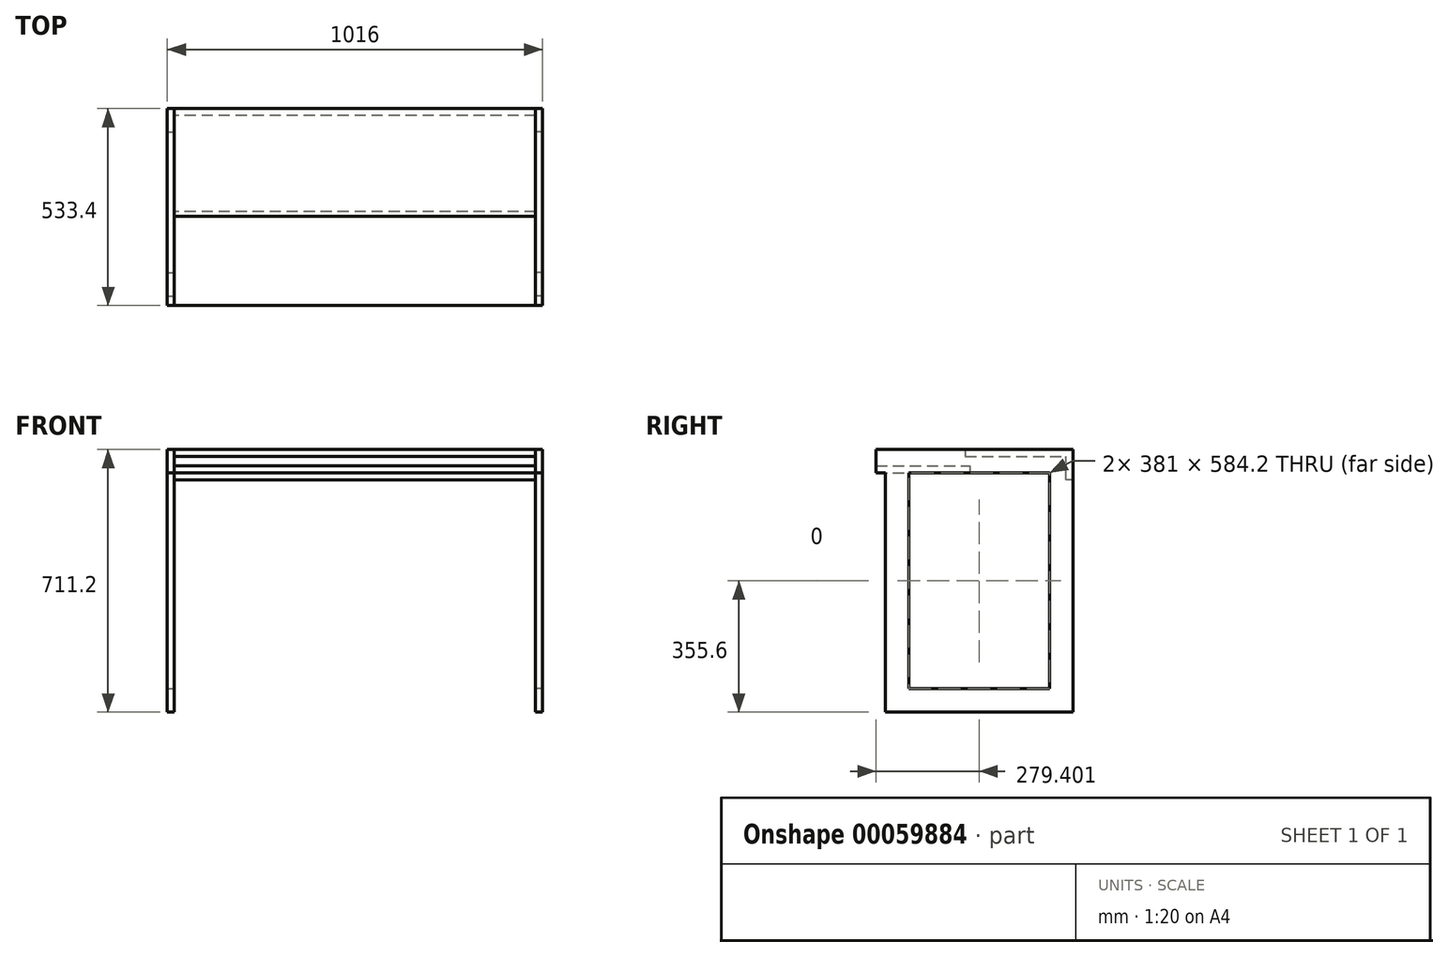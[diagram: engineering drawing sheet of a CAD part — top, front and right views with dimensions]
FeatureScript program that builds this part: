
annotation { "Feature Type Name" : "Feature", "Feature Type Description" : "" }
export const myFeature = defineFeature(function(context is Context, id is Id, definition is map)
    precondition{}
    {
        {
            var Q0;
            Q0=qCreatedBy(makeId("Right.planeOp"),FACE);
            var sketch = newSketch(context, id + "F0", { "sketchPlane" : qUnion([Q0])});
            skLineSegment(sketch, "E0.bottom", {"start": v(182.93, 112.04) * mm, "end": v(475.03, 112.04) * mm});
            skLineSegment(sketch, "E0.top", {"start": v(182.93, 92.99) * mm, "end": v(455.98, 92.99) * mm});
            skLineSegment(sketch, "E0.left", {"start": v(182.93, 112.04) * mm, "end": v(182.93, 92.99) * mm});
            skLineSegment(sketch, "E0.right", {"start": v(475.03, 112.04) * mm, "end": v(475.03, 29.49) * mm});
            skLineSegment(sketch, "E1.bottom", {"start": v(-58.37, 67.59) * mm, "end": v(195.63, 67.59) * mm});
            skLineSegment(sketch, "E1.top", {"start": v(-58.37, 48.54) * mm, "end": v(195.63, 48.54) * mm});
            skLineSegment(sketch, "E1.left", {"start": v(-58.37, 67.59) * mm, "end": v(-58.37, 48.54) * mm});
            skLineSegment(sketch, "E1.right", {"start": v(195.63, 67.59) * mm, "end": v(195.63, 48.54) * mm});
            skLineSegment(sketch, "E2", {"start": v(475.03, 29.49) * mm, "end": v(455.98, 29.49) * mm});
            skLineSegment(sketch, "E3", {"start": v(455.98, 29.49) * mm, "end": v(455.98, 92.99) * mm});
            skSolve(sketch);
        }
        {
            var Q0;
            Q0=makeQuery(id+"F0.imprint","IMPRINT",FACE,{"disambiguationData":[TD([[makeQuery(id+"F0.imprint","IMPRINT",EDGE,{"derivedFrom":sQuery(id+"F0.wireOp",EDGE,"E0.bottom")}),-1.0]])]});
            var Q1;
            Q1=makeQuery(id+"F0.imprint","IMPRINT",FACE,{"disambiguationData":[TD([[makeQuery(id+"F0.imprint","IMPRINT",EDGE,{"derivedFrom":sQuery(id+"F0.wireOp",EDGE,"E1.bottom")}),-1.0]])]});
            extrude(context, id + "F1", {"entities" : qUnion([Q0, Q1]), "depth" : 488.95 * mm, "hasSecondDirection" : true, "secondDirectionOppositeDirection" : true, "secondDirectionDepth" : 488.95 * mm});
        }
        {
            var Q0;
            Q0=makeQuery(id+"F1.opExtrude","CAP_FACE",FACE,{"disambiguationData":[OSD([sQuery(id+"F0.wireOp",EDGE,"E0.bottom"),sQuery(id+"F0.wireOp",EDGE,"E0.top"),sQuery(id+"F0.wireOp",EDGE,"E0.left"),sQuery(id+"F0.wireOp",EDGE,"E0.right"),sQuery(id+"F0.wireOp",EDGE,"E2"),sQuery(id+"F0.wireOp",EDGE,"E3")])],"isStart":false});
            var sketch = newSketch(context, id + "F2", { "sketchPlane" : qUnion([Q0])});
            skLineSegment(sketch, "E4.bottom", {"start": v(-58.37, 112.04) * mm, "end": v(475.03, 112.04) * mm});
            skLineSegment(sketch, "E4.top", {"start": v(-32.97, -599.16) * mm, "end": v(475.03, -599.16) * mm});
            skLineSegment(sketch, "E4.left", {"start": v(-58.37, 112.04) * mm, "end": v(-58.37, 48.54) * mm});
            skLineSegment(sketch, "E4.right", {"start": v(475.03, 112.04) * mm, "end": v(475.03, -599.16) * mm});
            skLineSegment(sketch, "E5.top", {"start": v(30.53, -535.66) * mm, "end": v(411.53, -535.66) * mm});
            skLineSegment(sketch, "E5.left", {"start": v(30.53, 48.54) * mm, "end": v(30.53, -535.66) * mm});
            skLineSegment(sketch, "E5.right", {"start": v(411.53, 48.54) * mm, "end": v(411.53, -535.66) * mm});
            skLineSegment(sketch, "E6", {"start": v(30.53, 48.54) * mm, "end": v(411.53, 48.54) * mm});
            skPoint(sketch, "E7.orphan", {"position": v(30.53, 0) * mm});
            skLineSegment(sketch, "E8", {"start": v(-32.97, -599.16) * mm, "end": v(-32.97, 48.54) * mm});
            skLineSegment(sketch, "E9", {"start": v(-32.97, 48.54) * mm, "end": v(-58.37, 48.54) * mm});
            skSolve(sketch);
        }
        {
            var Q0;
            Q0 = qSketchRegion(id + "F2", true);
            extrude(context, id + "F3", {"entities" : qUnion([Q0]), "depth" : 19.05 * mm});
        }
        {
            var Q0;
            Q0=makeQuery(id+"F1.opExtrude","CAP_FACE",FACE,{"disambiguationData":[OSD([sQuery(id+"F0.wireOp",EDGE,"E0.bottom"),sQuery(id+"F0.wireOp",EDGE,"E0.top"),sQuery(id+"F0.wireOp",EDGE,"E0.left"),sQuery(id+"F0.wireOp",EDGE,"E0.right"),sQuery(id+"F0.wireOp",EDGE,"E2"),sQuery(id+"F0.wireOp",EDGE,"E3")])],"isStart":true});
            var sketch = newSketch(context, id + "F4", { "sketchPlane" : qUnion([Q0])});
            skLineSegment(sketch, "E10.bottom", {"start": v(-475.03, 112.04) * mm, "end": v(58.37, 112.04) * mm});
            skLineSegment(sketch, "E10.top", {"start": v(-475.03, -599.16) * mm, "end": v(32.97, -599.16) * mm});
            skLineSegment(sketch, "E10.left", {"start": v(-475.03, 112.04) * mm, "end": v(-475.03, -599.16) * mm});
            skLineSegment(sketch, "E10.right", {"start": v(58.37, 112.04) * mm, "end": v(58.37, 48.54) * mm});
            skLineSegment(sketch, "E11.top", {"start": v(-411.53, -535.66) * mm, "end": v(-30.53, -535.66) * mm});
            skLineSegment(sketch, "E11.left", {"start": v(-411.53, 48.54) * mm, "end": v(-411.53, -535.66) * mm});
            skLineSegment(sketch, "E11.right", {"start": v(-30.53, 48.54) * mm, "end": v(-30.53, -535.66) * mm});
            skLineSegment(sketch, "E12", {"start": v(-411.53, 48.54) * mm, "end": v(-30.53, 48.54) * mm});
            skLineSegment(sketch, "E13", {"start": v(58.37, 48.54) * mm, "end": v(32.97, 48.54) * mm});
            skLineSegment(sketch, "E14", {"start": v(32.97, 48.54) * mm, "end": v(32.97, -599.16) * mm});
            skSolve(sketch);
        }
        {
            var Q0;
            Q0 = qSketchRegion(id + "F4", true);
            extrude(context, id + "F5", {"entities" : qUnion([Q0]), "depth" : 19.05 * mm});
        }
    });
